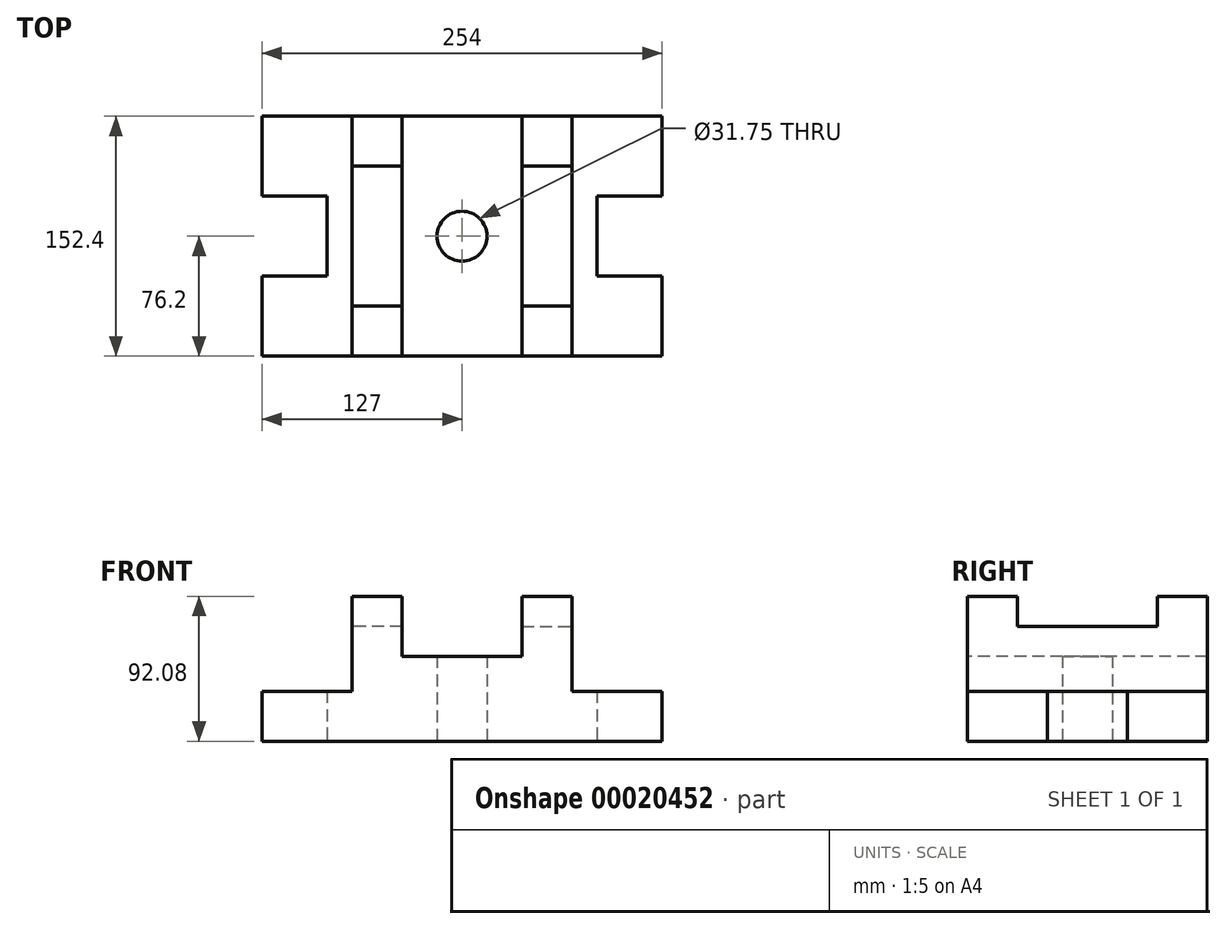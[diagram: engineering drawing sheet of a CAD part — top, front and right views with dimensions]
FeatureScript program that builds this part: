
annotation { "Feature Type Name" : "Feature", "Feature Type Description" : "" }
export const myFeature = defineFeature(function(context is Context, id is Id, definition is map)
    precondition{}
    {
        {
            var Q0;
            Q0=qCreatedBy(makeId("Top.planeOp"),FACE);
            var sketch = newSketch(context, id + "F0", { "sketchPlane" : qUnion([Q0])});
            skLineSegment(sketch, "E0.bottom", {"start": v(-61.29, -31.75) * mm, "end": v(65.71, -31.75) * mm});
            skLineSegment(sketch, "E0.top", {"start": v(-45.41, 44.45) * mm, "end": v(24.44, 44.45) * mm});
            skLineSegment(sketch, "E0.left", {"start": v(-61.29, -31.75) * mm, "end": v(-61.29, 28.58) * mm});
            skLineSegment(sketch, "E0.right", {"start": v(65.71, -31.75) * mm, "end": v(65.71, 19.05) * mm});
            skLineSegment(sketch, "E1.rect.top", {"start": v(24.44, 19.05) * mm, "end": v(65.71, 19.05) * mm});
            skLineSegment(sketch, "E1.rect.left", {"start": v(24.44, 44.45) * mm, "end": v(24.44, 19.05) * mm});
            skPoint(sketch, "E1.rect.middle", {"position": v(45.07, 31.75) * mm});
            skPoint(sketch, "E1.rect.right.start.orphan", {"position": v(65.71, 44.45) * mm});
            skLineSegment(sketch, "E2.bottom", {"start": v(-23.19, 0) * mm, "end": v(8.56, 0) * mm});
            skLineSegment(sketch, "E2.top", {"start": v(-23.19, -31.75) * mm, "end": v(8.56, -31.75) * mm});
            skLineSegment(sketch, "E2.left", {"start": v(-23.19, 0) * mm, "end": v(-23.19, -31.75) * mm});
            skLineSegment(sketch, "E2.right", {"start": v(8.56, 0) * mm, "end": v(8.56, -31.75) * mm});
            skLineSegment(sketch, "E3", {"start": v(-23.19, 0) * mm, "end": v(-23.19, 44.45) * mm});
            skLineSegment(sketch, "E4", {"start": v(8.56, 0) * mm, "end": v(8.56, 44.45) * mm});
            skArc(sketch, "E5", {"start": v(-61.29, 28.58) * mm, "mid": v(-50.06, 33.22) * mm, "end": v(-45.41, 44.45) * mm});
            skSolve(sketch);
        }
        {
            var Q0;
            {var subQ3=sQuery(id+"F0.wireOp",EDGE,"E0.right");Q0=makeQuery(id+"F0.imprint","IMPRINT",FACE,{"disambiguationData":[TD([[makeQuery(id+"F0.imprint","IMPRINT",EDGE,{"derivedFrom":subQ3}),1.0]])]});}
            extrude(context, id + "F1", {"entities" : qUnion([Q0]), "depth" : 31.75 * mm});
        }
        {
            var Q0;
            Q0=makeQuery(id+"F0.imprint","IMPRINT",FACE,{"disambiguationData":[TD([[makeQuery(id+"F0.imprint","IMPRINT",EDGE,{"derivedFrom":sQuery(id+"F0.wireOp",EDGE,"E2.bottom")}),-1.0]])]});
            extrude(context, id + "F2", {"entities" : qUnion([Q0]), "operationType" : NewBodyOperationType.ADD, "depth" : 92.07 * mm});
        }
        {
            var Q0;
            {var subQ3=sQuery(id+"F0.wireOp",EDGE,"E0.left");Q0=makeQuery(id+"F0.imprint","IMPRINT",FACE,{"disambiguationData":[TD([[makeQuery(id+"F0.imprint","IMPRINT",EDGE,{"derivedFrom":subQ3}),-1.0]])]});}
            extrude(context, id + "F3", {"entities" : qUnion([Q0]), "operationType" : NewBodyOperationType.ADD, "depth" : 53.97 * mm});
        }
        {
            var Q0;
            Q0=makeQuery(id+"F0.imprint","IMPRINT",FACE,{"disambiguationData":[TD([[makeQuery(id+"F0.imprint","IMPRINT",EDGE,{"derivedFrom":sQuery(id+"F0.wireOp",EDGE,"E2.bottom")}),1.0]])]});
            extrude(context, id + "F4", {"entities" : qUnion([Q0]), "operationType" : NewBodyOperationType.ADD, "depth" : 73.02 * mm});
        }
        {
            var Q0;
            Q0=makeQuery(id+"F1.opExtrude","SWEPT_BODY",BODY,{"disambiguationData":[OSD([sQuery(id+"F0.wireOp",EDGE,"E0.bottom"),sQuery(id+"F0.wireOp",EDGE,"E0.top"),sQuery(id+"F0.wireOp",EDGE,"E0.right"),sQuery(id+"F0.wireOp",EDGE,"E1.rect.top"),sQuery(id+"F0.wireOp",EDGE,"E1.rect.left"),sQuery(id+"F0.wireOp",EDGE,"E2.right"),sQuery(id+"F0.wireOp",EDGE,"E4")])]});
            var Q1;
            {var subQ0=sQuery(id+"F0.wireOp",EDGE,"E0.top");Q1=makeQuery(id+"F4.boolean.opBoolean","MERGE",FACE,{"derivedFrom":[makeQuery(id+"F1.opExtrude","SWEPT_FACE",FACE,{"disambiguationData":[OSD([subQ0])]}),makeQuery(id+"F3.opExtrude","SWEPT_FACE",FACE,{"disambiguationData":[OSD([subQ0])]}),makeQuery(id+"F4.opExtrude","SWEPT_FACE",FACE,{"disambiguationData":[OSD([subQ0])]})]});}
            mirror(context, id + "F5", {"operationType" : NewBodyOperationType.ADD, "entities" : qUnion([Q0]), "mirrorPlane" : qUnion([Q1])});
        }
        {
            var Q0;
            Q0=makeQuery(id+"F1.opExtrude","SWEPT_BODY",BODY,{"disambiguationData":[OSD([sQuery(id+"F0.wireOp",EDGE,"E0.bottom"),sQuery(id+"F0.wireOp",EDGE,"E0.top"),sQuery(id+"F0.wireOp",EDGE,"E0.right"),sQuery(id+"F0.wireOp",EDGE,"E1.rect.top"),sQuery(id+"F0.wireOp",EDGE,"E1.rect.left"),sQuery(id+"F0.wireOp",EDGE,"E2.right"),sQuery(id+"F0.wireOp",EDGE,"E4")])]});
            var Q1;
            Q1=makeQuery(id+"F5.opPattern","COPY",FACE,{"derivedFrom":makeQuery(id+"F3.opExtrude","SWEPT_FACE",FACE,{"disambiguationData":[OSD([sQuery(id+"F0.wireOp",EDGE,"E0.left")])]}),"instanceName":"1"});
            mirror(context, id + "F6", {"operationType" : NewBodyOperationType.ADD, "entities" : qUnion([Q0]), "mirrorPlane" : qUnion([Q1])});
        }
    });
